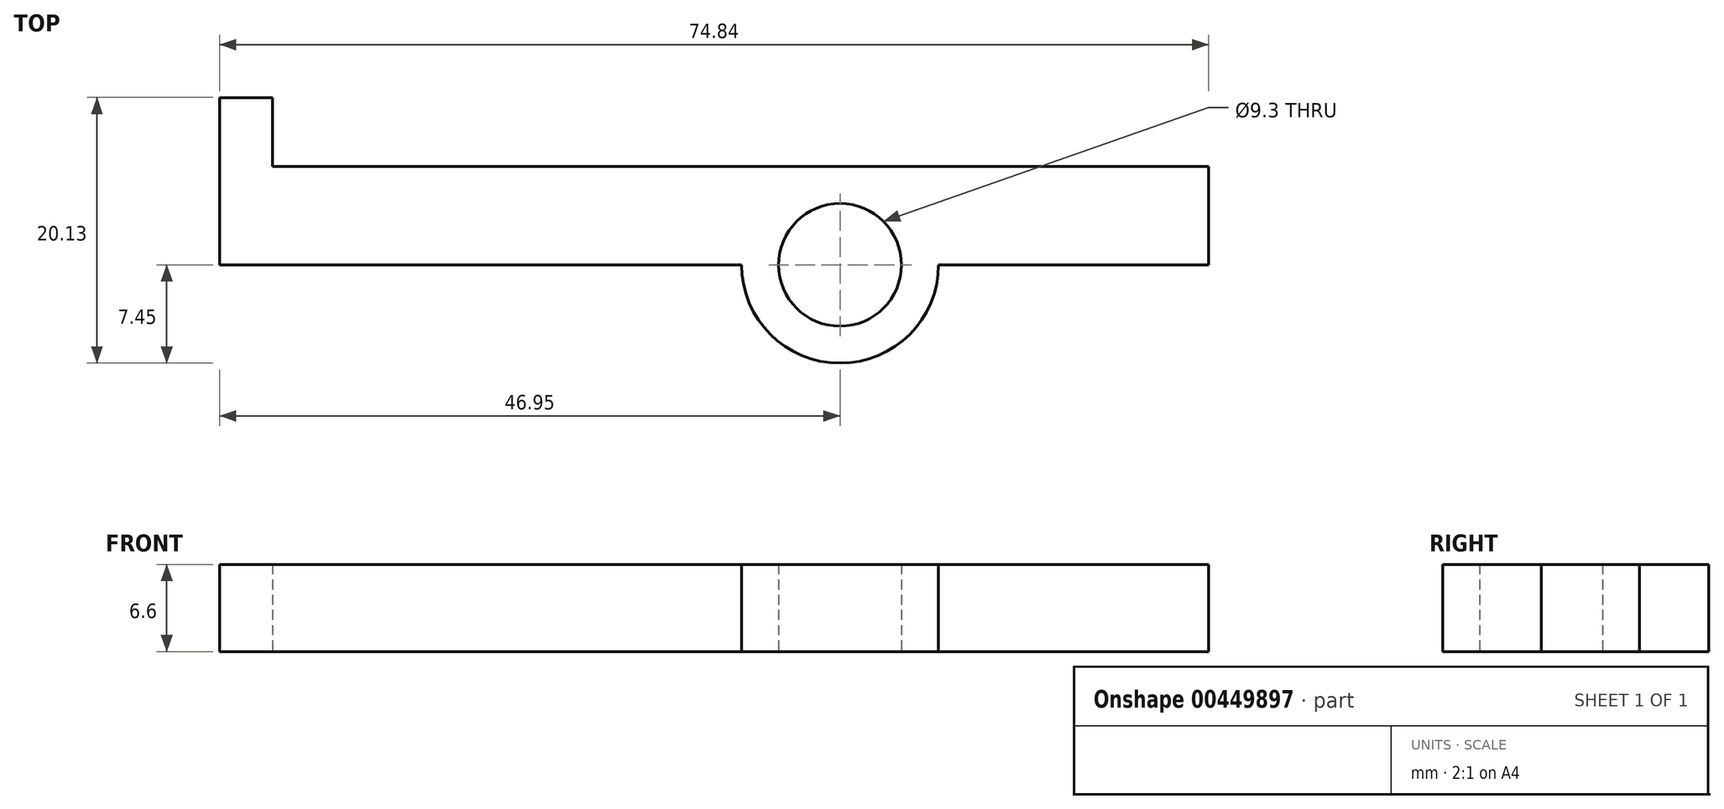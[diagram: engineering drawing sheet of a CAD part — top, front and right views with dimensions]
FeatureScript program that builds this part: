
annotation { "Feature Type Name" : "Feature", "Feature Type Description" : "" }
export const myFeature = defineFeature(function(context is Context, id is Id, definition is map)
    precondition{}
    {
        {
            var Q0;
            Q0=qCreatedBy(makeId("Top.planeOp"),FACE);
            var sketch = newSketch(context, id + "F0", { "sketchPlane" : qUnion([Q0])});
            skCircle(sketch, "E0", {"center": v(0, 0) * mm, "radius": 4.65 * mm});
            skCircle(sketch, "E1", {"center": v(0, 0) * mm, "radius": 7.45 * mm});
            skLineSegment(sketch, "E2", {"start": v(0, 7.45) * mm, "end": v(-42.95, 7.45) * mm});
            skLineSegment(sketch, "E3", {"start": v(-42.95, 7.45) * mm, "end": v(-42.95, 0) * mm});
            skLineSegment(sketch, "E4", {"start": v(-42.95, 0) * mm, "end": v(-7.45, 0) * mm});
            skLineSegment(sketch, "E5.bottom", {"start": v(0, 7.45) * mm, "end": v(27.89, 7.45) * mm});
            skLineSegment(sketch, "E5.top", {"start": v(0, 0) * mm, "end": v(27.89, 0) * mm});
            skLineSegment(sketch, "E5.left", {"start": v(0, 7.45) * mm, "end": v(0, 0) * mm});
            skLineSegment(sketch, "E5.right", {"start": v(27.89, 7.45) * mm, "end": v(27.89, 0) * mm});
            skSolve(sketch);
        }
        {
            var Q0;
            Q0 = qSketchRegion(id + "F0", true);
            extrude(context, id + "F1", {"entities" : qUnion([Q0]), "depth" : 6.6 * mm, "offsetDistance" : 25 * mm});
        }
        {
            var Q0;
            Q0=makeQuery(id+"F1.opExtrude","SWEPT_FACE",FACE,{"disambiguationData":[OSD([sQuery(id+"F0.wireOp",EDGE,"E3")])]});
            var sketch = newSketch(context, id + "F2", { "sketchPlane" : qUnion([Q0])});
            skLineSegment(sketch, "E6.bottom", {"start": v(0, 6.6) * mm, "end": v(-12.68, 6.6) * mm});
            skLineSegment(sketch, "E6.top", {"start": v(0, 0) * mm, "end": v(-12.68, 0) * mm});
            skLineSegment(sketch, "E6.left", {"start": v(0, 6.6) * mm, "end": v(0, 0) * mm});
            skLineSegment(sketch, "E6.right", {"start": v(-12.68, 6.6) * mm, "end": v(-12.68, 0) * mm});
            skSolve(sketch);
        }
        {
            var Q0;
            Q0 = qSketchRegion(id + "F2", true);
            extrude(context, id + "F3", {"entities" : qUnion([Q0]), "operationType" : NewBodyOperationType.ADD, "depth" : 4 * mm, "offsetDistance" : 25 * mm});
        }
    });
